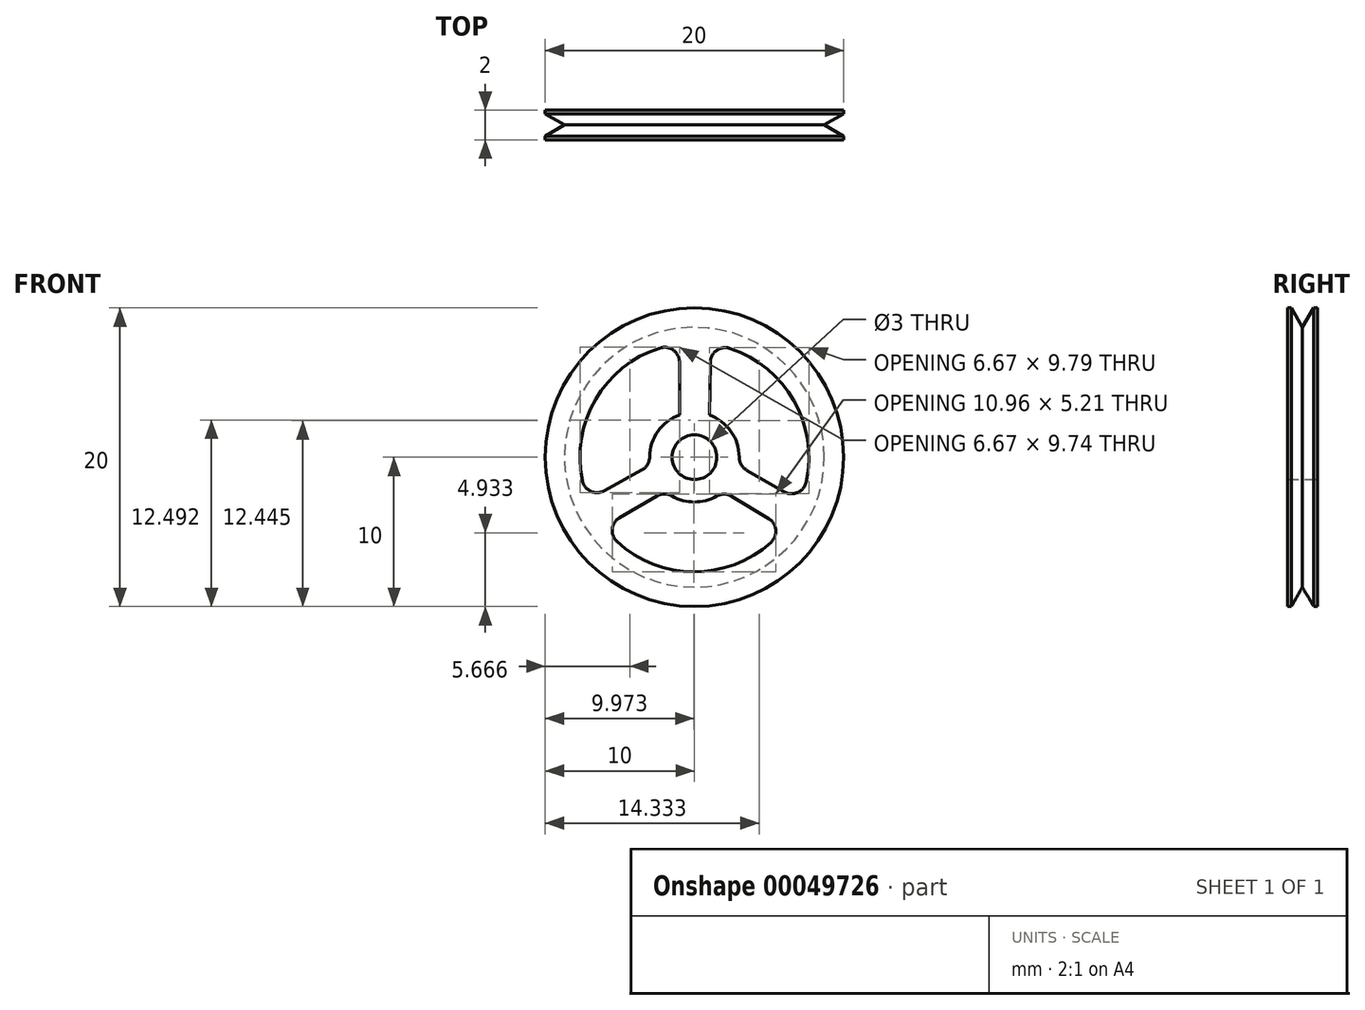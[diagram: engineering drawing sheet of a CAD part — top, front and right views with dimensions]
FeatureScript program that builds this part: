
annotation { "Feature Type Name" : "Feature", "Feature Type Description" : "" }
export const myFeature = defineFeature(function(context is Context, id is Id, definition is map)
    precondition{}
    {
        {
            var Q0;
            Q0=qCreatedBy(makeId("Front.planeOp"),FACE);
            var sketch = newSketch(context, id + "F0", { "sketchPlane" : qUnion([Q0])});
            skArc(sketch, "E0.0", {"start": v(-2.3, 7.32) * mm, "mid": v(-6.62, 3.87) * mm, "end": v(-7.5, -1.58) * mm});
            skArc(sketch, "E1", {"start": v(-1, 2.83) * mm, "mid": v(-2.45, 1.74) * mm, "end": v(-3, 0.01) * mm});
            skCircle(sketch, "E2", {"center": v(0, 0) * mm, "radius": 1.5 * mm});
            skPoint(sketch, "E3.start.orphan", {"position": v(0, 10) * mm});
            skPoint(sketch, "E4.trimOffspring.end.orphan", {"position": v(-2, 0.63) * mm});
            skPoint(sketch, "E5.MirrorCS.start.orphan", {"position": v(-2, 10) * mm});
            skLineSegment(sketch, "E6", {"start": v(-1, 6.36) * mm, "end": v(-1, 2.83) * mm});
            skLineSegment(sketch, "E7.MirrorCS", {"start": v(1.07, 6.36) * mm, "end": v(1, 2.83) * mm});
            skPoint(sketch, "E8.orphan", {"position": v(1.1, 7.6) * mm});
            skPoint(sketch, "E9.orphan", {"position": v(1, 2.83) * mm});
            skPoint(sketch, "E10.trimOffspring.end.orphan", {"position": v(0, 0.63) * mm});
            skPoint(sketch, "E11.MirrorCS.end.orphan", {"position": v(1, 0.63) * mm});
            skPoint(sketch, "E12.trimOffspring.end.orphan", {"position": v(-1, 0.63) * mm});
            skPoint(sketch, "E13.0.start.orphan", {"position": v(-1, 10) * mm});
            skPoint(sketch, "E14.MirrorCS.start.orphan", {"position": v(1, 10) * mm});
            skCircle(sketch, "E15", {"center": v(0, 0) * mm, "radius": 10 * mm});
            skLineSegment(sketch, "E16.1.0", {"start": v(-5.01, -4.05) * mm, "end": v(-2.5, -2.6) * mm});
            skLineSegment(sketch, "E16.1.1", {"start": v(-6.04, -2.25) * mm, "end": v(-3.52, -0.86) * mm});
            skLineSegment(sketch, "E16.2.0", {"start": v(6.01, -2.32) * mm, "end": v(3.5, -0.87) * mm});
            skLineSegment(sketch, "E16.2.1", {"start": v(4.97, -4.1) * mm, "end": v(2.5, -2.62) * mm});
            skArc(sketch, "E17.trimOffspring", {"start": v(3, 0) * mm, "mid": v(2.45, 1.73) * mm, "end": v(1, 2.83) * mm});
            skArc(sketch, "E18.trimOffspring", {"start": v(7.49, -1.67) * mm, "mid": v(6.66, 3.8) * mm, "end": v(2.38, 7.3) * mm});
            skArc(sketch, "E19.trimOffspring", {"start": v(-1.5, -2.6) * mm, "mid": v(0, -3) * mm, "end": v(1.5, -2.6) * mm});
            skArc(sketch, "E20.trimOffspring", {"start": v(-5.19, -5.65) * mm, "mid": v(-0.04, -7.67) * mm, "end": v(5.12, -5.7) * mm});
            skPoint(sketch, "E21.visualSharp", {"position": v(-1, 7.6) * mm});
            skArc(sketch, "E21.filletArc", {"start": v(-1, 6.36) * mm, "mid": v(-1.4, 7.17) * mm, "end": v(-2.3, 7.32) * mm});
            skPoint(sketch, "E22.visualSharp", {"position": v(-2.95, -0.55) * mm});
            skArc(sketch, "E22.filletArc", {"start": v(-3.52, -0.86) * mm, "mid": v(-3.14, -0.5) * mm, "end": v(-3, 0.01) * mm});
            skPoint(sketch, "E23.visualSharp", {"position": v(-7.12, -2.85) * mm});
            skArc(sketch, "E23.filletArc", {"start": v(-7.5, -1.58) * mm, "mid": v(-6.94, -2.29) * mm, "end": v(-6.04, -2.25) * mm});
            skArc(sketch, "E24.filletArc", {"start": v(2.38, 7.3) * mm, "mid": v(1.5, 7.16) * mm, "end": v(1.07, 6.36) * mm});
            skPoint(sketch, "E25.visualSharp", {"position": v(7.09, -2.94) * mm});
            skArc(sketch, "E25.filletArc", {"start": v(6.01, -2.32) * mm, "mid": v(6.91, -2.37) * mm, "end": v(7.49, -1.67) * mm});
            skPoint(sketch, "E26.visualSharp", {"position": v(2.95, -0.55) * mm});
            skArc(sketch, "E26.filletArc", {"start": v(3, 0) * mm, "mid": v(3.13, -0.5) * mm, "end": v(3.5, -0.87) * mm});
            skPoint(sketch, "E27.visualSharp", {"position": v(1.95, -2.28) * mm});
            skArc(sketch, "E27.filletArc", {"start": v(2.5, -2.62) * mm, "mid": v(2, -2.47) * mm, "end": v(1.5, -2.6) * mm});
            skPoint(sketch, "E28.visualSharp", {"position": v(-1.95, -2.28) * mm});
            skArc(sketch, "E28.filletArc", {"start": v(-1.5, -2.6) * mm, "mid": v(-2, -2.46) * mm, "end": v(-2.5, -2.6) * mm});
            skPoint(sketch, "E29.visualSharp", {"position": v(-6.09, -4.67) * mm});
            skArc(sketch, "E29.filletArc", {"start": v(-5.01, -4.05) * mm, "mid": v(-5.5, -4.8) * mm, "end": v(-5.19, -5.65) * mm});
            skPoint(sketch, "E30.visualSharp", {"position": v(6.03, -4.74) * mm});
            skArc(sketch, "E30.filletArc", {"start": v(5.12, -5.7) * mm, "mid": v(5.45, -4.87) * mm, "end": v(4.97, -4.1) * mm});
            skSolve(sketch);
        }
        {
            var Q0;
            Q0=makeQuery(id+"F0.imprint","IMPRINT",FACE,{"disambiguationData":[TD([[makeQuery(id+"F0.imprint","IMPRINT",EDGE,{"derivedFrom":sQuery(id+"F0.wireOp",EDGE,"E0.0")}),-1.0]])]});
            extrude(context, id + "F1", {"entities" : qUnion([Q0]), "endBound" : BoundingType.SYMMETRIC, "depth" : 2 * mm});
        }
        {
            var Q0;
            Q0=qCreatedBy(makeId("Right.planeOp"),FACE);
            var sketch = newSketch(context, id + "F2", { "sketchPlane" : qUnion([Q0])});
            skLineSegment(sketch, "E31", {"start": v(0, 10) * mm, "end": v(0, 8.7) * mm});
            skLineSegment(sketch, "E32", {"start": v(0, 10) * mm, "end": v(-0.75, 10) * mm});
            skLineSegment(sketch, "E33", {"start": v(-0.75, 10) * mm, "end": v(0, 8.7) * mm});
            skLineSegment(sketch, "E34.MirrorCS", {"start": v(0, 10) * mm, "end": v(0.75, 10) * mm});
            skLineSegment(sketch, "E35.MirrorCS", {"start": v(0.75, 10) * mm, "end": v(0, 8.7) * mm});
            skLineSegment(sketch, "E36", {"start": v(7, 0) * mm, "end": v(-8.36, 0) * mm, "construction": true});
            skPoint(sketch, "E37.start.orphan", {"position": v(18.07, 9.79) * mm});
            skPoint(sketch, "E38.orphan", {"position": v(19.2, 8.88) * mm});
            skPoint(sketch, "E39.end.orphan", {"position": v(16.94, 10.7) * mm});
            skSolve(sketch);
        }
        {
            var Q0;
            Q0 = qSketchRegion(id + "F2", true);
            var Q1;
            Q1=sQuery(id+"F2.wireOp",EDGE,"E36");
            revolve(context, id + "F3", {"operationType" : NewBodyOperationType.REMOVE, "entities" : qUnion([Q0]), "axis" : qUnion([Q1]), "revolveType" : RevolveType.FULL, "oppositeDirection" : true});
        }
    });
